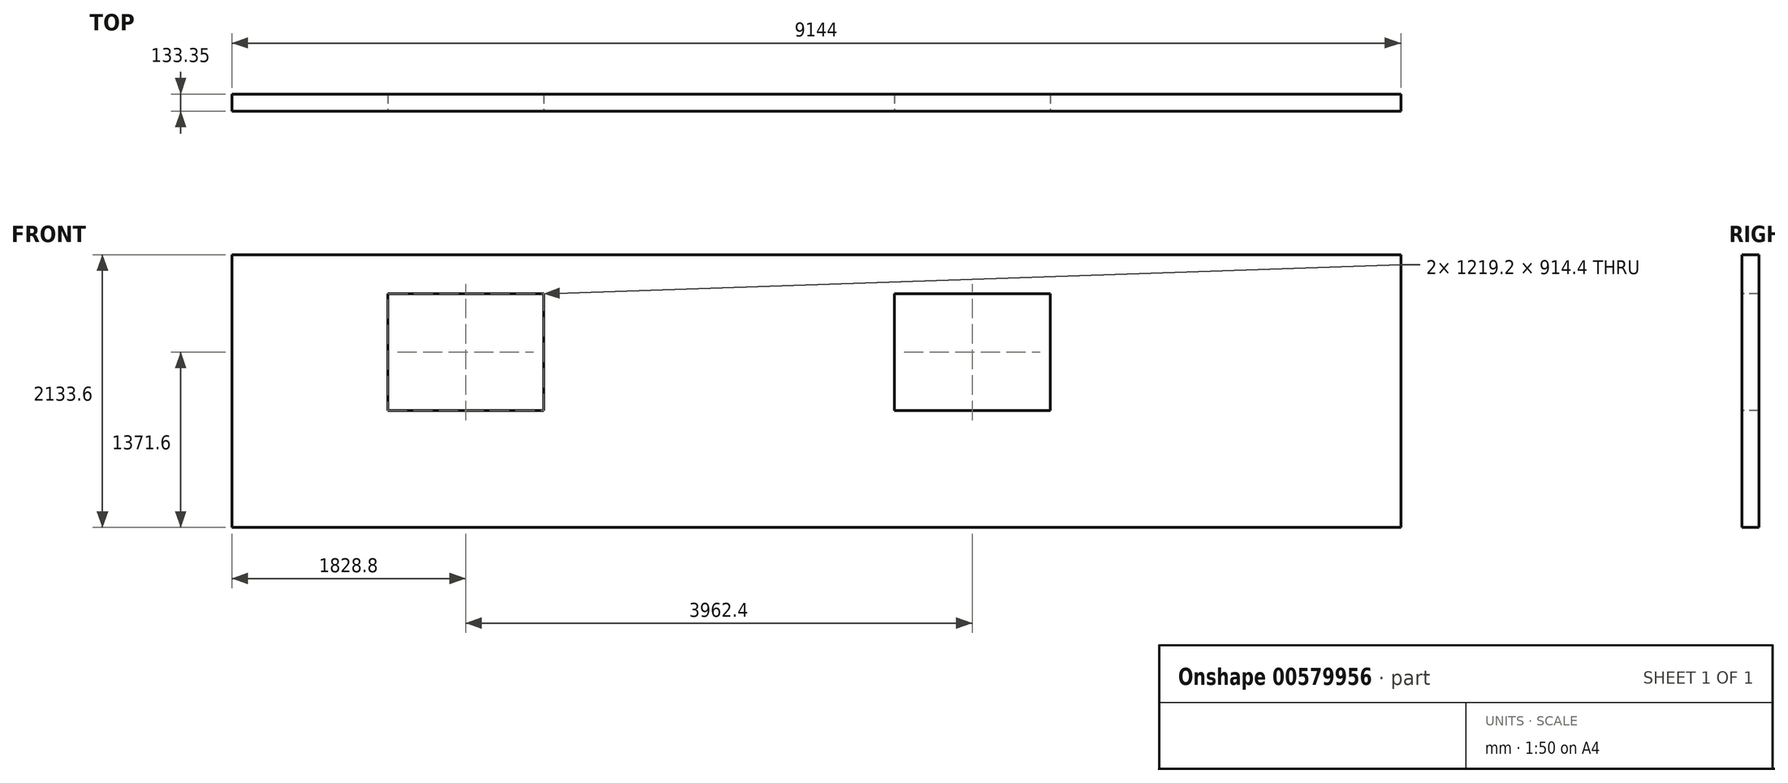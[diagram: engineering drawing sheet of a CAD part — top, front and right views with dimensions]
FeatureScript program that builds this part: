
annotation { "Feature Type Name" : "Feature", "Feature Type Description" : "" }
export const myFeature = defineFeature(function(context is Context, id is Id, definition is map)
    precondition{}
    {
        {
            var Q0;
            Q0=qCreatedBy(makeId("Top.planeOp"),FACE);
            var sketch = newSketch(context, id + "F0", { "sketchPlane" : qUnion([Q0])});
            skLineSegment(sketch, "E0.bottom", {"start": v(-1080.53, 93.25) * mm, "end": v(8063.47, 93.25) * mm});
            skLineSegment(sketch, "E0.top", {"start": v(-1080.53, -40.1) * mm, "end": v(8063.47, -40.1) * mm});
            skLineSegment(sketch, "E0.left", {"start": v(-1080.53, 93.25) * mm, "end": v(-1080.53, -40.1) * mm});
            skLineSegment(sketch, "E0.right", {"start": v(8063.47, 93.25) * mm, "end": v(8063.47, -40.1) * mm});
            skSolve(sketch);
        }
        {
            var Q0;
            Q0=makeQuery(id+"F0.imprint","IMPRINT",FACE,{"disambiguationData":[TD([[makeQuery(id+"F0.imprint","IMPRINT",EDGE,{"derivedFrom":sQuery(id+"F0.wireOp",EDGE,"E0.bottom")}),-1.0]])]});
            extrude(context, id + "F1", {"entities" : qUnion([Q0]), "depth" : 2133.6 * mm, "offsetDistance" : 25.4 * mm});
        }
        {
            var Q0;
            Q0=makeQuery(id+"F1.opExtrude","SWEPT_FACE",FACE,{"disambiguationData":[OSD([sQuery(id+"F0.wireOp",EDGE,"E0.top")])]});
            var sketch = newSketch(context, id + "F2", { "sketchPlane" : qUnion([Q0])});
            skPoint(sketch, "E1.left.start.orphan", {"position": v(0, 1676.4) * mm});
            skLineSegment(sketch, "E2.bottom", {"start": v(138.67, 1828.8) * mm, "end": v(1357.87, 1828.8) * mm});
            skLineSegment(sketch, "E2.top", {"start": v(138.67, 914.4) * mm, "end": v(1357.87, 914.4) * mm});
            skLineSegment(sketch, "E2.left", {"start": v(138.67, 1828.8) * mm, "end": v(138.67, 914.4) * mm});
            skLineSegment(sketch, "E2.right", {"start": v(1357.87, 1828.8) * mm, "end": v(1357.87, 914.4) * mm});
            skLineSegment(sketch, "E3.bottom", {"start": v(4101.07, 1828.79) * mm, "end": v(5320.27, 1828.79) * mm});
            skLineSegment(sketch, "E3.top", {"start": v(4101.07, 914.39) * mm, "end": v(5320.27, 914.39) * mm});
            skLineSegment(sketch, "E3.left", {"start": v(4101.07, 1828.79) * mm, "end": v(4101.07, 914.39) * mm});
            skLineSegment(sketch, "E3.right", {"start": v(5320.27, 1828.79) * mm, "end": v(5320.27, 914.39) * mm});
            skSolve(sketch);
        }
        {
            var Q0;
            Q0 = qSketchRegion(id + "F2", true);
            extrude(context, id + "F3", {"entities" : qUnion([Q0]), "operationType" : NewBodyOperationType.REMOVE, "oppositeDirection" : true, "depth" : 203.2 * mm, "offsetDistance" : 25.4 * mm});
        }
    });
